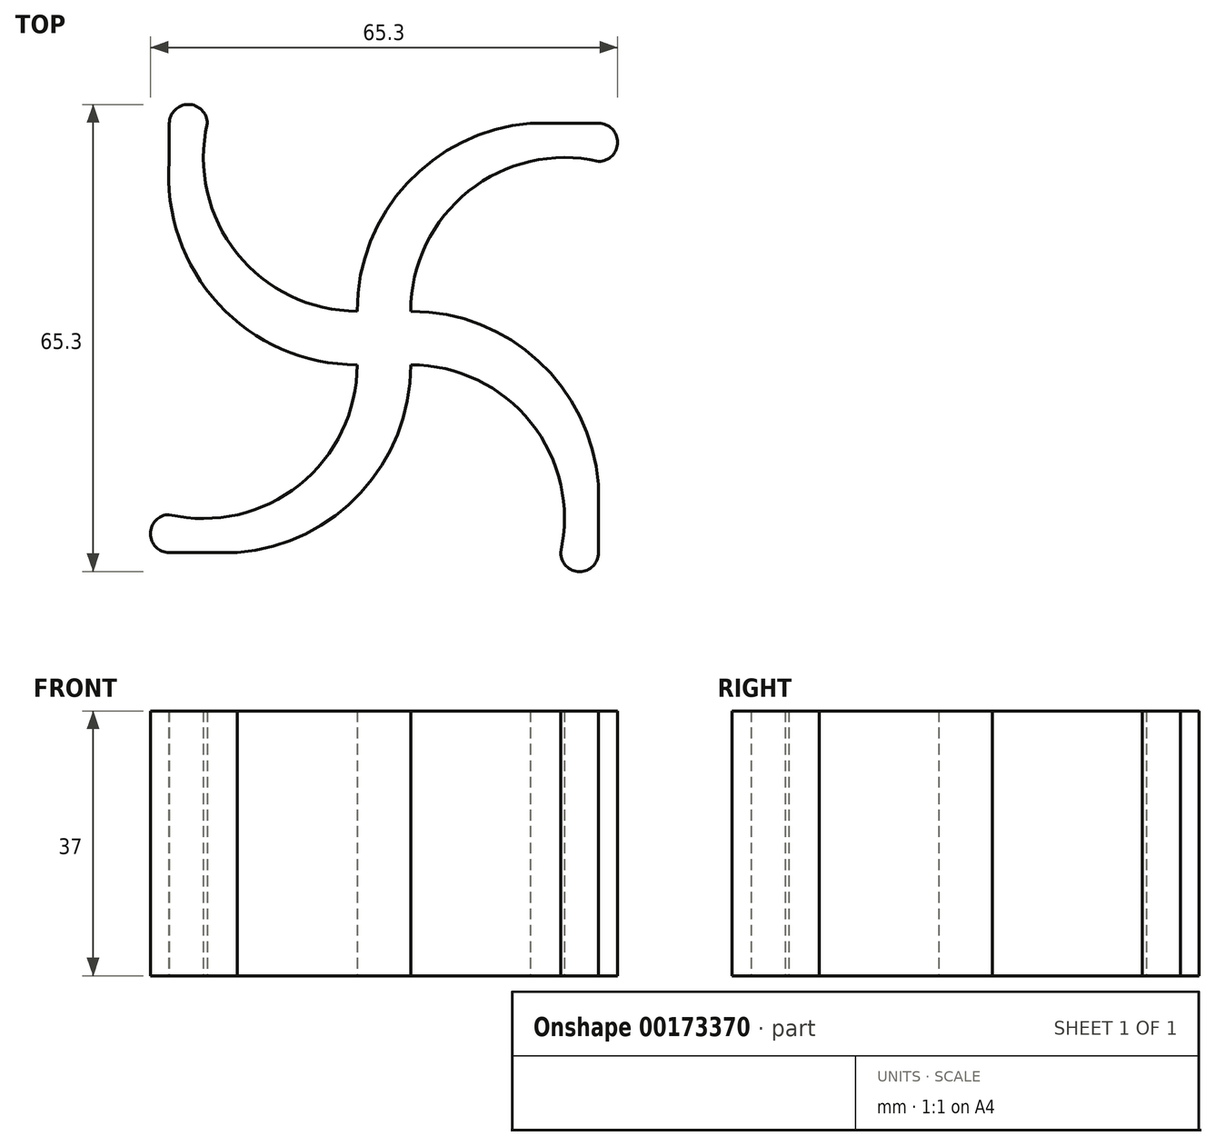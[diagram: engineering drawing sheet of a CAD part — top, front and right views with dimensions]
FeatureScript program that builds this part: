
annotation { "Feature Type Name" : "Feature", "Feature Type Description" : "" }
export const myFeature = defineFeature(function(context is Context, id is Id, definition is map)
    precondition{}
    {
        {
            var Q0;
            Q0=qCreatedBy(makeId("Top.planeOp"),FACE);
            var sketch = newSketch(context, id + "F0", { "sketchPlane" : qUnion([Q0])});
            skLineSegment(sketch, "E0.left", {"start": v(30, 30) * mm, "end": v(30, 24.7) * mm, "construction": true});
            skLineSegment(sketch, "E0.right", {"start": v(-30, 24.7) * mm, "end": v(-30, 20.48) * mm, "construction": true});
            skPoint(sketch, "E0.middle", {"position": v(0, 0) * mm});
            skPoint(sketch, "E1", {"position": v(30, 24.7) * mm});
            skPoint(sketch, "E2", {"position": v(24.7, 30) * mm});
            skPoint(sketch, "E3", {"position": v(-24.7, 30) * mm});
            skPoint(sketch, "E4", {"position": v(-30, 24.7) * mm});
            skPoint(sketch, "E5", {"position": v(-30, -24.7) * mm});
            skPoint(sketch, "E6", {"position": v(-24.7, -30) * mm});
            skPoint(sketch, "E7", {"position": v(30, -24.7) * mm});
            skPoint(sketch, "E8", {"position": v(24.7, -30) * mm});
            skArc(sketch, "E9", {"start": v(20.47, 30) * mm, "mid": v(3.23, 21.6) * mm, "end": v(-3.75, 3.75) * mm});
            skArc(sketch, "E10", {"start": v(30, 24.7) * mm, "mid": v(11.83, 20.54) * mm, "end": v(3.75, 3.75) * mm});
            skArc(sketch, "E11", {"start": v(-20.48, -30) * mm, "mid": v(-3.23, -21.61) * mm, "end": v(3.75, -3.75) * mm});
            skArc(sketch, "E12", {"start": v(-30, -24.7) * mm, "mid": v(-11.83, -20.54) * mm, "end": v(-3.75, -3.75) * mm});
            skArc(sketch, "E13", {"start": v(24.7, -30) * mm, "mid": v(20.54, -11.83) * mm, "end": v(3.75, -3.75) * mm});
            skArc(sketch, "E14", {"start": v(30, -20.47) * mm, "mid": v(21.6, -3.23) * mm, "end": v(3.75, 3.75) * mm});
            skArc(sketch, "E15", {"start": v(-30, 24.7) * mm, "mid": v(-23.1, 4.72) * mm, "end": v(-3.75, -3.75) * mm});
            skPoint(sketch, "E16.orphan", {"position": v(-30, 30) * mm});
            skPoint(sketch, "E17.orphan", {"position": v(3.75, -30) * mm});
            skPoint(sketch, "E18.trimOffspring.end.orphan", {"position": v(-3.75, -30) * mm});
            skPoint(sketch, "E19.right.end.orphan", {"position": v(-30, -3.75) * mm});
            skPoint(sketch, "E19.right.start.orphan", {"position": v(-30, 3.75) * mm});
            skPoint(sketch, "E19.left.start.orphan", {"position": v(30, 3.75) * mm});
            skPoint(sketch, "E20.orphan", {"position": v(30, -3.75) * mm});
            skPoint(sketch, "E0.top.start.orphan", {"position": v(30, -30) * mm});
            skPoint(sketch, "E21.bottom.start.orphan", {"position": v(3.75, 30) * mm});
            skLineSegment(sketch, "E22.trimOffspring", {"start": v(3.75, 30) * mm, "end": v(-3.75, 30) * mm, "construction": true});
            skLineSegment(sketch, "E23", {"start": v(-30, 30) * mm, "end": v(-30, 24.7) * mm});
            skLineSegment(sketch, "E24", {"start": v(-24.7, -30) * mm, "end": v(-20.48, -30) * mm});
            skLineSegment(sketch, "E25", {"start": v(20.47, 30) * mm, "end": v(24.7, 30) * mm});
            skLineSegment(sketch, "E26", {"start": v(30, -20.47) * mm, "end": v(30, -24.7) * mm});
            skPoint(sketch, "E27.trimOffspring.end.orphan", {"position": v(-30, -30) * mm});
            skArc(sketch, "E28", {"start": v(-24.7, 30) * mm, "mid": v(-20.54, 11.83) * mm, "end": v(-3.75, 3.75) * mm});
            skLineSegment(sketch, "E29", {"start": v(24.7, 30) * mm, "end": v(30, 30) * mm});
            skLineSegment(sketch, "E30", {"start": v(30, -24.7) * mm, "end": v(30, -30) * mm});
            skLineSegment(sketch, "E31", {"start": v(-24.7, -30) * mm, "end": v(-30, -30) * mm});
            skArc(sketch, "E32", {"start": v(-30, -24.7) * mm, "mid": v(-32.65, -27.35) * mm, "end": v(-30, -30) * mm});
            skArc(sketch, "E33", {"start": v(24.7, -30) * mm, "mid": v(27.35, -32.65) * mm, "end": v(30, -30) * mm});
            skArc(sketch, "E34", {"start": v(30, 24.7) * mm, "mid": v(32.65, 27.35) * mm, "end": v(30, 30) * mm});
            skArc(sketch, "E35", {"start": v(-24.7, 30) * mm, "mid": v(-27.35, 32.65) * mm, "end": v(-30, 30) * mm});
            skSolve(sketch);
        }
        {
            var Q0;
            Q0 = qSketchRegion(id + "F0", true);
            extrude(context, id + "F1", {"entities" : qUnion([Q0]), "depth" : 37 * mm});
        }
    });
